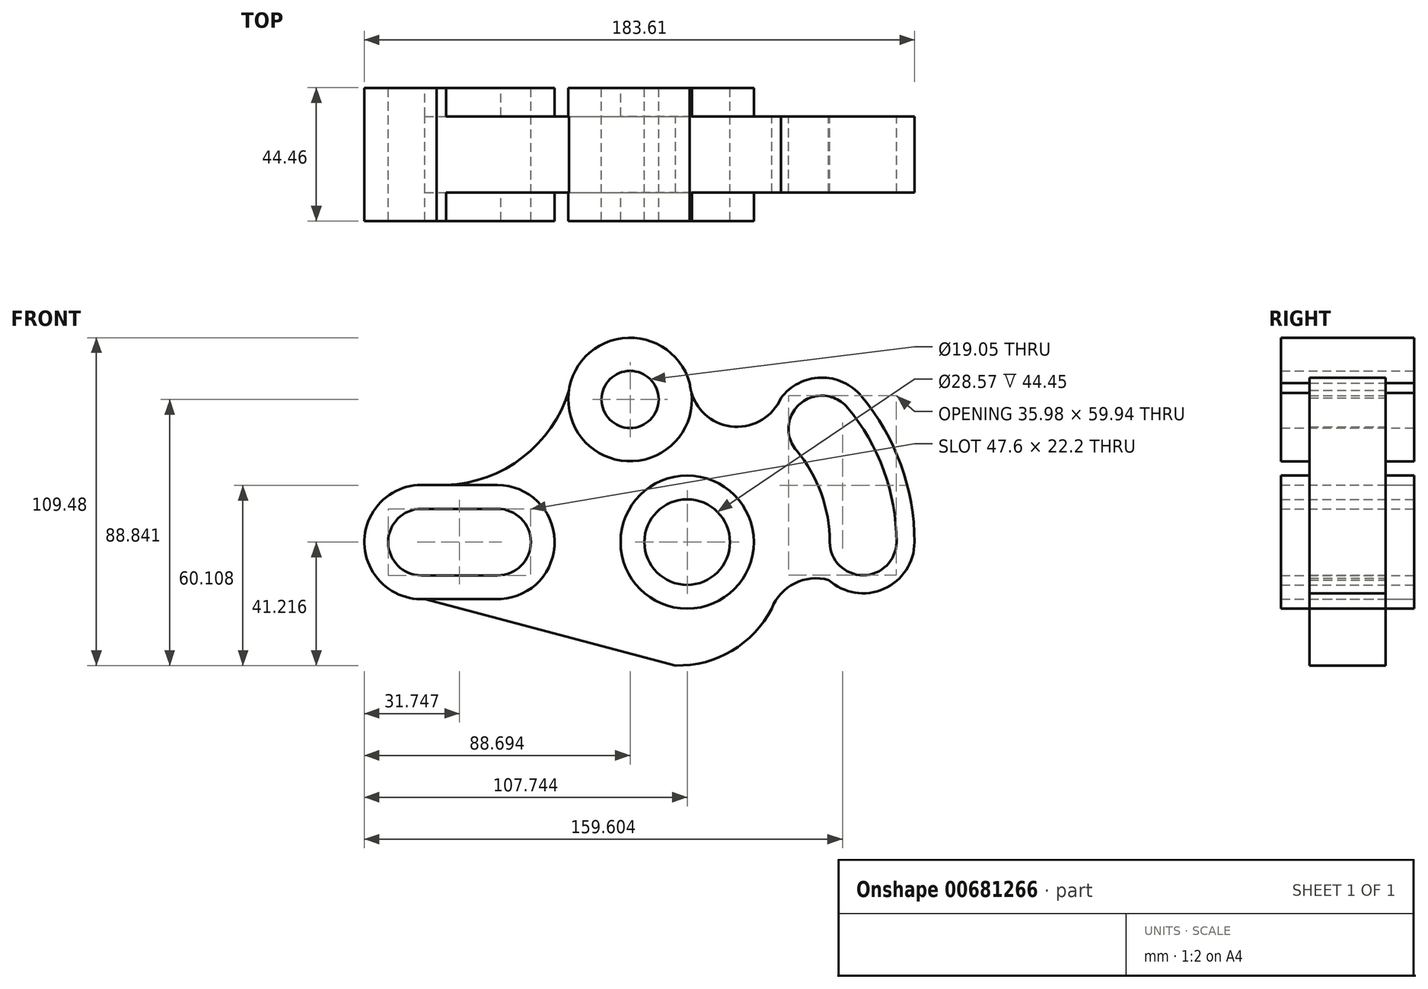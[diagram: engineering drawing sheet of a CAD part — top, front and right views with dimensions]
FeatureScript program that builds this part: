
annotation { "Feature Type Name" : "Feature", "Feature Type Description" : "" }
export const myFeature = defineFeature(function(context is Context, id is Id, definition is map)
    precondition{}
    {
        {
            var Q0;
            Q0=qCreatedBy(makeId("Front.planeOp"),FACE);
            var sketch = newSketch(context, id + "F0", { "sketchPlane" : qUnion([Q0])});
            skLineSegment(sketch, "E0", {"start": v(-62.24, 6.22) * mm, "end": v(-36.84, 6.22) * mm});
            skLineSegment(sketch, "E1", {"start": v(-62.24, 28.42) * mm, "end": v(-36.84, 28.42) * mm});
            skArc(sketch, "E2", {"start": v(-62.24, 28.42) * mm, "mid": v(-73.34, 17.32) * mm, "end": v(-62.24, 6.22) * mm});
            skArc(sketch, "E3", {"start": v(-36.84, 6.22) * mm, "mid": v(-25.74, 17.32) * mm, "end": v(-36.84, 28.42) * mm});
            skLineSegment(sketch, "E4", {"start": v(-61.16, -1.7) * mm, "end": v(-35.76, -1.7) * mm});
            skArc(sketch, "E5", {"start": v(-62.24, 36.37) * mm, "mid": v(-81.29, 16.77) * mm, "end": v(-61.16, -1.7) * mm});
            skArc(sketch, "E6", {"start": v(-35.76, -1.7) * mm, "mid": v(-17.8, 17.86) * mm, "end": v(-36.84, 36.37) * mm});
            skCircle(sketch, "E7", {"center": v(7.4, 64.94) * mm, "radius": 20.64 * mm});
            skCircle(sketch, "E8", {"center": v(7.4, 64.94) * mm, "radius": 9.53 * mm});
            skCircle(sketch, "E9", {"center": v(26.45, 17.32) * mm, "radius": 22.23 * mm});
            skCircle(sketch, "E10", {"center": v(26.45, 17.32) * mm, "radius": 14.29 * mm});
            skPoint(sketch, "E11.visualSharp", {"position": v(-0.86, 36.37) * mm});
            skLineSegment(sketch, "E12", {"start": v(-62.24, 36.37) * mm, "end": v(-36.84, 36.37) * mm});
            skLineSegment(sketch, "E13", {"start": v(26.45, 17.32) * mm, "end": v(120, 95.82) * mm, "construction": true});
            skLineSegment(sketch, "E14", {"start": v(26.45, 17.32) * mm, "end": v(148.81, 17.32) * mm, "construction": true});
            skArc(sketch, "E15", {"start": v(74.05, 17.32) * mm, "mid": v(85.18, 6.24) * mm, "end": v(96.3, 17.32) * mm});
            skArc(sketch, "E16", {"start": v(74.05, 17.32) * mm, "mid": v(71.18, 33.6) * mm, "end": v(62.92, 47.91) * mm});
            skArc(sketch, "E17", {"start": v(96.3, 17.32) * mm, "mid": v(92.1, 41.2) * mm, "end": v(79.96, 62.21) * mm});
            skArc(sketch, "E18", {"start": v(79.96, 62.21) * mm, "mid": v(64.26, 63.62) * mm, "end": v(62.92, 47.91) * mm});
            skArc(sketch, "E19.0", {"start": v(84.58, 66.08) * mm, "mid": v(71, 72.24) * mm, "end": v(57.72, 65.42) * mm});
            skArc(sketch, "E19.1", {"start": v(102.32, 17.3) * mm, "mid": v(97.75, 43.25) * mm, "end": v(84.58, 66.08) * mm});
            skArc(sketch, "E19.2", {"start": v(73.67, 4.66) * mm, "mid": v(92.1, 1.68) * mm, "end": v(102.32, 17.3) * mm});
            skLineSegment(sketch, "E20", {"start": v(-61.16, -1.7) * mm, "end": v(22.61, -23.88) * mm});
            skArc(sketch, "E21", {"start": v(22.61, -23.88) * mm, "mid": v(41.38, -19.01) * mm, "end": v(54.65, -4.88) * mm});
            skArc(sketch, "E22", {"start": v(73.67, 4.66) * mm, "mid": v(62.33, 3.54) * mm, "end": v(54.65, -4.88) * mm});
            skArc(sketch, "E23", {"start": v(27.31, 70.38) * mm, "mid": v(40.58, 56.01) * mm, "end": v(57.72, 65.42) * mm});
            skArc(sketch, "E24", {"start": v(-57.17, 36.37) * mm, "mid": v(-29.69, 44.66) * mm, "end": v(-13, 68.02) * mm});
            skSolve(sketch);
        }
        {
            var Q0;
            Q0=makeQuery(id+"F0.imprint","IMPRINT",FACE,{"disambiguationData":[TD([[makeQuery(id+"F0.imprint","IMPRINT",EDGE,{"derivedFrom":sQuery(id+"F0.wireOp",EDGE,"E4")}),-1.0]])]});
            extrude(context, id + "F1", {"entities" : qUnion([Q0]), "endBound" : BoundingType.SYMMETRIC, "depth" : 25.4 * mm, "offsetDistance" : 25.4 * mm});
        }
        {
            var Q0;
            Q0=makeQuery(id+"F0.imprint","IMPRINT",FACE,{"disambiguationData":[TD([[makeQuery(id+"F0.imprint","IMPRINT",EDGE,{"derivedFrom":sQuery(id+"F0.wireOp",EDGE,"E8")}),-1.0]])]});
            var Q1;
            Q1=makeQuery(id+"F0.imprint","IMPRINT",FACE,{"disambiguationData":[TD([[makeQuery(id+"F0.imprint","IMPRINT",EDGE,{"derivedFrom":sQuery(id+"F0.wireOp",EDGE,"E0")}),-1.0]])]});
            var Q2;
            Q2=makeQuery(id+"F0.imprint","IMPRINT",FACE,{"disambiguationData":[TD([[makeQuery(id+"F0.imprint","IMPRINT",EDGE,{"derivedFrom":sQuery(id+"F0.wireOp",EDGE,"E9")}),1.0]])]});
            extrude(context, id + "F2", {"entities" : qUnion([Q0, Q1, Q2]), "operationType" : NewBodyOperationType.ADD, "endBound" : BoundingType.SYMMETRIC, "depth" : 44.45 * mm, "offsetDistance" : 25.4 * mm});
        }
    });
